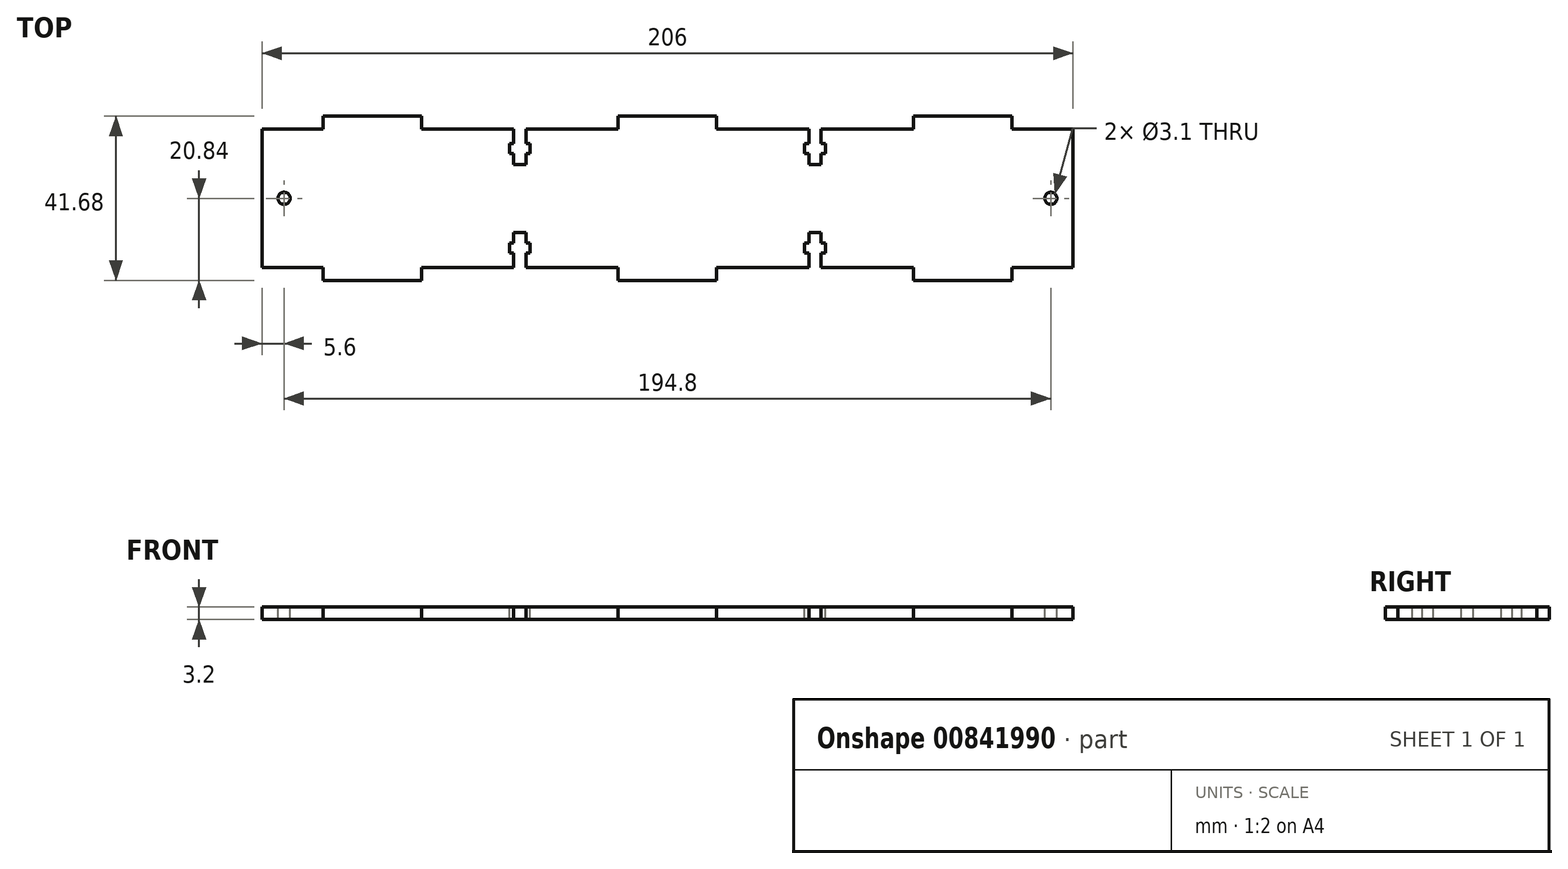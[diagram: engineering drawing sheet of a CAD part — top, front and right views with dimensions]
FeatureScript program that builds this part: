
annotation { "Feature Type Name" : "Feature", "Feature Type Description" : "" }
export const myFeature = defineFeature(function(context is Context, id is Id, definition is map)
    precondition{}
    {
        {
            assignVariable(context, id + "F0", {"name" : "mat_t", "anyValue" : 3.2});
        }
        {
            var Q0;
            Q0=qCreatedBy(makeId("Top.planeOp"),FACE);
            var sketch = newSketch(context, id + "F1", { "sketchPlane" : qUnion([Q0])});
            skLineSegment(sketch, "E0.bottom", {"start": v(103, -17.64) * mm, "end": v(-103, -17.64) * mm});
            skLineSegment(sketch, "E0.top", {"start": v(103, 17.64) * mm, "end": v(-103, 17.64) * mm});
            skLineSegment(sketch, "E0.left", {"start": v(103, -17.64) * mm, "end": v(103, 17.64) * mm});
            skLineSegment(sketch, "E0.right", {"start": v(-103, -17.64) * mm, "end": v(-103, 17.64) * mm});
            skPoint(sketch, "E0.middle", {"position": v(0, 0) * mm});
            skSolve(sketch);
        }
        {
            var Q0;
            Q0 = qSketchRegion(id + "F1", true);
            extrude(context, id + "F2", {"entities" : qUnion([Q0]), "depth" : (getVariable(context, 'mat_t')) * mm, "offsetDistance" : 25 * mm});
        }
        {
            var Q0;
            Q0=makeQuery(id+"F2.opExtrude","CAP_FACE",FACE,{"disambiguationData":[OSD([sQuery(id+"F1.wireOp",EDGE,"E0.bottom"),sQuery(id+"F1.wireOp",EDGE,"E0.top"),sQuery(id+"F1.wireOp",EDGE,"E0.left"),sQuery(id+"F1.wireOp",EDGE,"E0.right")])],"isStart":false});
            var sketch = newSketch(context, id + "F3", { "sketchPlane" : qUnion([Q0])});
            skLineSegment(sketch, "E1", {"start": v(-103, 0) * mm, "end": v(103, 0) * mm, "construction": true});
            skLineSegment(sketch, "E2", {"start": v(0, 17.64) * mm, "end": v(0, -17.64) * mm, "construction": true});
            skLineSegment(sketch, "E3.bottom", {"start": v(-87.5, -17.64) * mm, "end": v(-62.5, -17.64) * mm});
            skLineSegment(sketch, "E3.top", {"start": v(-87.5, -20.84) * mm, "end": v(-62.5, -20.84) * mm});
            skLineSegment(sketch, "E3.left", {"start": v(-87.5, -17.64) * mm, "end": v(-87.5, -20.84) * mm});
            skLineSegment(sketch, "E3.right", {"start": v(-62.5, -17.64) * mm, "end": v(-62.5, -20.84) * mm});
            skLineSegment(sketch, "E4.bottom", {"start": v(-12.5, -17.64) * mm, "end": v(12.5, -17.64) * mm});
            skLineSegment(sketch, "E4.top", {"start": v(-12.5, -20.84) * mm, "end": v(12.5, -20.84) * mm});
            skLineSegment(sketch, "E4.left", {"start": v(-12.5, -17.64) * mm, "end": v(-12.5, -20.84) * mm});
            skLineSegment(sketch, "E4.right", {"start": v(12.5, -17.64) * mm, "end": v(12.5, -20.84) * mm});
            skLineSegment(sketch, "E5.MirrorCS", {"start": v(87.5, -20.84) * mm, "end": v(62.5, -20.84) * mm});
            skLineSegment(sketch, "E6.MirrorCS", {"start": v(87.5, -17.64) * mm, "end": v(62.5, -17.64) * mm});
            skLineSegment(sketch, "E7.MirrorCS", {"start": v(87.5, -17.64) * mm, "end": v(87.5, -20.84) * mm});
            skLineSegment(sketch, "E8.MirrorCS", {"start": v(62.5, -17.64) * mm, "end": v(62.5, -20.84) * mm});
            skLineSegment(sketch, "E9", {"start": v(-75, -17.64) * mm, "end": v(-75, -20.84) * mm, "construction": true});
            skLineSegment(sketch, "E10", {"start": v(75, -17.64) * mm, "end": v(75, -20.84) * mm, "construction": true});
            skLineSegment(sketch, "E11.MirrorCS", {"start": v(75, 17.64) * mm, "end": v(75, 20.84) * mm, "construction": true});
            skLineSegment(sketch, "E12.MirrorCS", {"start": v(87.5, 17.64) * mm, "end": v(62.5, 17.64) * mm});
            skLineSegment(sketch, "E13.MirrorCS", {"start": v(-87.5, 17.64) * mm, "end": v(-62.5, 17.64) * mm});
            skLineSegment(sketch, "E14.MirrorCS", {"start": v(-12.5, 17.64) * mm, "end": v(-12.5, 20.84) * mm});
            skLineSegment(sketch, "E15.MirrorCS", {"start": v(-75, 17.64) * mm, "end": v(-75, 20.84) * mm, "construction": true});
            skLineSegment(sketch, "E16.MirrorCS", {"start": v(-12.5, 17.64) * mm, "end": v(12.5, 17.64) * mm});
            skLineSegment(sketch, "E17.MirrorCS", {"start": v(-87.5, 17.64) * mm, "end": v(-87.5, 20.84) * mm});
            skLineSegment(sketch, "E18.MirrorCS", {"start": v(62.5, 17.64) * mm, "end": v(62.5, 20.84) * mm});
            skLineSegment(sketch, "E19.MirrorCS", {"start": v(-87.5, 20.84) * mm, "end": v(-62.5, 20.84) * mm});
            skLineSegment(sketch, "E20.MirrorCS", {"start": v(12.5, 17.64) * mm, "end": v(12.5, 20.84) * mm});
            skLineSegment(sketch, "E21.MirrorCS", {"start": v(87.5, 20.84) * mm, "end": v(62.5, 20.84) * mm});
            skLineSegment(sketch, "E22.MirrorCS", {"start": v(-62.5, 17.64) * mm, "end": v(-62.5, 20.84) * mm});
            skLineSegment(sketch, "E23.MirrorCS", {"start": v(-12.5, 20.84) * mm, "end": v(12.5, 20.84) * mm});
            skLineSegment(sketch, "E24.MirrorCS", {"start": v(87.5, 17.64) * mm, "end": v(87.5, 20.84) * mm});
            skSolve(sketch);
        }
        {
            var Q0;
            Q0 = qSketchRegion(id + "F3", true);
            var Q1;
            Q1=makeQuery(id+"F2.opExtrude","CAP_FACE",FACE,{"disambiguationData":[OSD([sQuery(id+"F1.wireOp",EDGE,"E0.bottom"),sQuery(id+"F1.wireOp",EDGE,"E0.top"),sQuery(id+"F1.wireOp",EDGE,"E0.left"),sQuery(id+"F1.wireOp",EDGE,"E0.right")])],"isStart":true});
            extrude(context, id + "F4", {"entities" : qUnion([Q0]), "operationType" : NewBodyOperationType.ADD, "endBound" : BoundingType.UP_TO_SURFACE, "oppositeDirection" : true, "depth" : 25 * mm, "endBoundEntityFace" : qUnion([Q1]), "offsetDistance" : 25 * mm});
        }
        {
            var Q0;
            Q0=makeQuery(id+"F2.opExtrude","CAP_FACE",FACE,{"disambiguationData":[OSD([sQuery(id+"F1.wireOp",EDGE,"E0.bottom"),sQuery(id+"F1.wireOp",EDGE,"E0.top"),sQuery(id+"F1.wireOp",EDGE,"E0.left"),sQuery(id+"F1.wireOp",EDGE,"E0.right")])],"isStart":false});
            var sketch = newSketch(context, id + "F5", { "sketchPlane" : qUnion([Q0])});
            skLineSegment(sketch, "E25", {"start": v(0, 20.84) * mm, "end": v(0, -20.84) * mm, "construction": true});
            skLineSegment(sketch, "E26", {"start": v(-97.4, 17.64) * mm, "end": v(-97.4, -17.64) * mm, "construction": true});
            skCircle(sketch, "E27", {"center": v(-97.4, 0) * mm, "radius": 1.55 * mm});
            skCircle(sketch, "E28.MirrorC", {"center": v(97.4, 0) * mm, "radius": 1.55 * mm});
            skLineSegment(sketch, "E29.bottom", {"start": v(-35.95, -17.64) * mm, "end": v(-35.95, -8.64) * mm});
            skLineSegment(sketch, "E29.top", {"start": v(-39.05, -17.64) * mm, "end": v(-39.05, -8.64) * mm});
            skLineSegment(sketch, "E29.left", {"start": v(-35.95, -17.64) * mm, "end": v(-39.05, -17.64) * mm});
            skLineSegment(sketch, "E29.right", {"start": v(-35.95, -8.64) * mm, "end": v(-39.05, -8.64) * mm});
            skLineSegment(sketch, "E30", {"start": v(-37.5, -17.64) * mm, "end": v(-37.5, -8.64) * mm, "construction": true});
            skLineSegment(sketch, "E31.bottom", {"start": v(-34.85, -11.4) * mm, "end": v(-34.85, -13.9) * mm});
            skLineSegment(sketch, "E31.top", {"start": v(-40.15, -11.4) * mm, "end": v(-40.15, -13.9) * mm});
            skLineSegment(sketch, "E31.left", {"start": v(-34.85, -11.4) * mm, "end": v(-40.15, -11.4) * mm});
            skLineSegment(sketch, "E31.right", {"start": v(-34.85, -13.9) * mm, "end": v(-40.15, -13.9) * mm});
            skPoint(sketch, "E31.middle", {"position": v(-37.5, -12.64) * mm});
            skLineSegment(sketch, "E32.MirrorCS", {"start": v(35.95, -17.64) * mm, "end": v(39.05, -17.64) * mm});
            skLineSegment(sketch, "E33.MirrorCS", {"start": v(34.85, -11.4) * mm, "end": v(34.85, -13.9) * mm});
            skLineSegment(sketch, "E34.MirrorCS", {"start": v(40.15, -11.39) * mm, "end": v(40.15, -13.89) * mm});
            skLineSegment(sketch, "E35.MirrorCS", {"start": v(35.95, -8.64) * mm, "end": v(39.05, -8.64) * mm});
            skLineSegment(sketch, "E36.MirrorCS", {"start": v(34.85, -11.4) * mm, "end": v(40.15, -11.39) * mm});
            skLineSegment(sketch, "E37.MirrorCS", {"start": v(34.85, -13.9) * mm, "end": v(40.15, -13.9) * mm});
            skLineSegment(sketch, "E38.MirrorCS", {"start": v(35.95, -17.64) * mm, "end": v(35.95, -8.64) * mm});
            skPoint(sketch, "E39.MirrorP", {"position": v(37.5, -12.64) * mm});
            skLineSegment(sketch, "E40.MirrorCS", {"start": v(37.5, -17.64) * mm, "end": v(37.5, -8.64) * mm, "construction": true});
            skLineSegment(sketch, "E41.MirrorCS", {"start": v(39.05, -17.64) * mm, "end": v(39.05, -8.64) * mm});
            skLineSegment(sketch, "E42", {"start": v(-103, 0) * mm, "end": v(103, 0) * mm, "construction": true});
            skLineSegment(sketch, "E43.MirrorCS", {"start": v(-35.95, 8.64) * mm, "end": v(-39.05, 8.64) * mm});
            skLineSegment(sketch, "E44.MirrorCS", {"start": v(-35.95, 17.64) * mm, "end": v(-39.05, 17.64) * mm});
            skLineSegment(sketch, "E45.MirrorCS", {"start": v(40.15, 11.4) * mm, "end": v(40.15, 13.9) * mm});
            skLineSegment(sketch, "E46.MirrorCS", {"start": v(35.95, 17.64) * mm, "end": v(39.05, 17.64) * mm});
            skLineSegment(sketch, "E47.MirrorCS", {"start": v(-34.85, 11.4) * mm, "end": v(-34.85, 13.9) * mm});
            skLineSegment(sketch, "E48.MirrorCS", {"start": v(35.95, 8.64) * mm, "end": v(39.05, 8.64) * mm});
            skLineSegment(sketch, "E49.MirrorCS", {"start": v(-40.15, 11.4) * mm, "end": v(-40.15, 13.9) * mm});
            skLineSegment(sketch, "E50.MirrorCS", {"start": v(34.85, 11.4) * mm, "end": v(34.85, 13.9) * mm});
            skLineSegment(sketch, "E51.MirrorCS", {"start": v(34.85, 13.9) * mm, "end": v(40.15, 13.9) * mm});
            skLineSegment(sketch, "E52.MirrorCS", {"start": v(34.85, 11.4) * mm, "end": v(40.15, 11.4) * mm});
            skLineSegment(sketch, "E53.MirrorCS", {"start": v(-34.85, 11.39) * mm, "end": v(-40.15, 11.39) * mm});
            skLineSegment(sketch, "E54.MirrorCS", {"start": v(-34.85, 13.89) * mm, "end": v(-40.15, 13.89) * mm});
            skLineSegment(sketch, "E55.MirrorCS", {"start": v(35.95, 17.64) * mm, "end": v(35.95, 8.64) * mm});
            skLineSegment(sketch, "E56.MirrorCS", {"start": v(-37.5, 17.64) * mm, "end": v(-37.5, 8.64) * mm, "construction": true});
            skLineSegment(sketch, "E57.MirrorCS", {"start": v(-35.95, 17.64) * mm, "end": v(-35.95, 8.64) * mm});
            skPoint(sketch, "E58.MirrorP", {"position": v(-37.5, 12.64) * mm});
            skPoint(sketch, "E59.MirrorP", {"position": v(37.5, 12.64) * mm});
            skLineSegment(sketch, "E60.MirrorCS", {"start": v(-39.05, 17.64) * mm, "end": v(-39.05, 8.64) * mm});
            skLineSegment(sketch, "E61.MirrorCS", {"start": v(39.05, 17.64) * mm, "end": v(39.05, 8.64) * mm});
            skLineSegment(sketch, "E62.MirrorCS", {"start": v(37.5, 17.64) * mm, "end": v(37.5, 8.64) * mm, "construction": true});
            skPoint(sketch, "E63", {"position": v(0, 0) * mm});
            skPoint(sketch, "E64", {"position": v(0, -2.67) * mm});
            skSolve(sketch);
        }
        {
            var Q0;
            Q0 = qSketchRegion(id + "F5", true);
            extrude(context, id + "F6", {"entities" : qUnion([Q0]), "operationType" : NewBodyOperationType.REMOVE, "endBound" : BoundingType.THROUGH_ALL, "oppositeDirection" : true, "depth" : 25 * mm, "offsetDistance" : 25 * mm});
        }
    });
